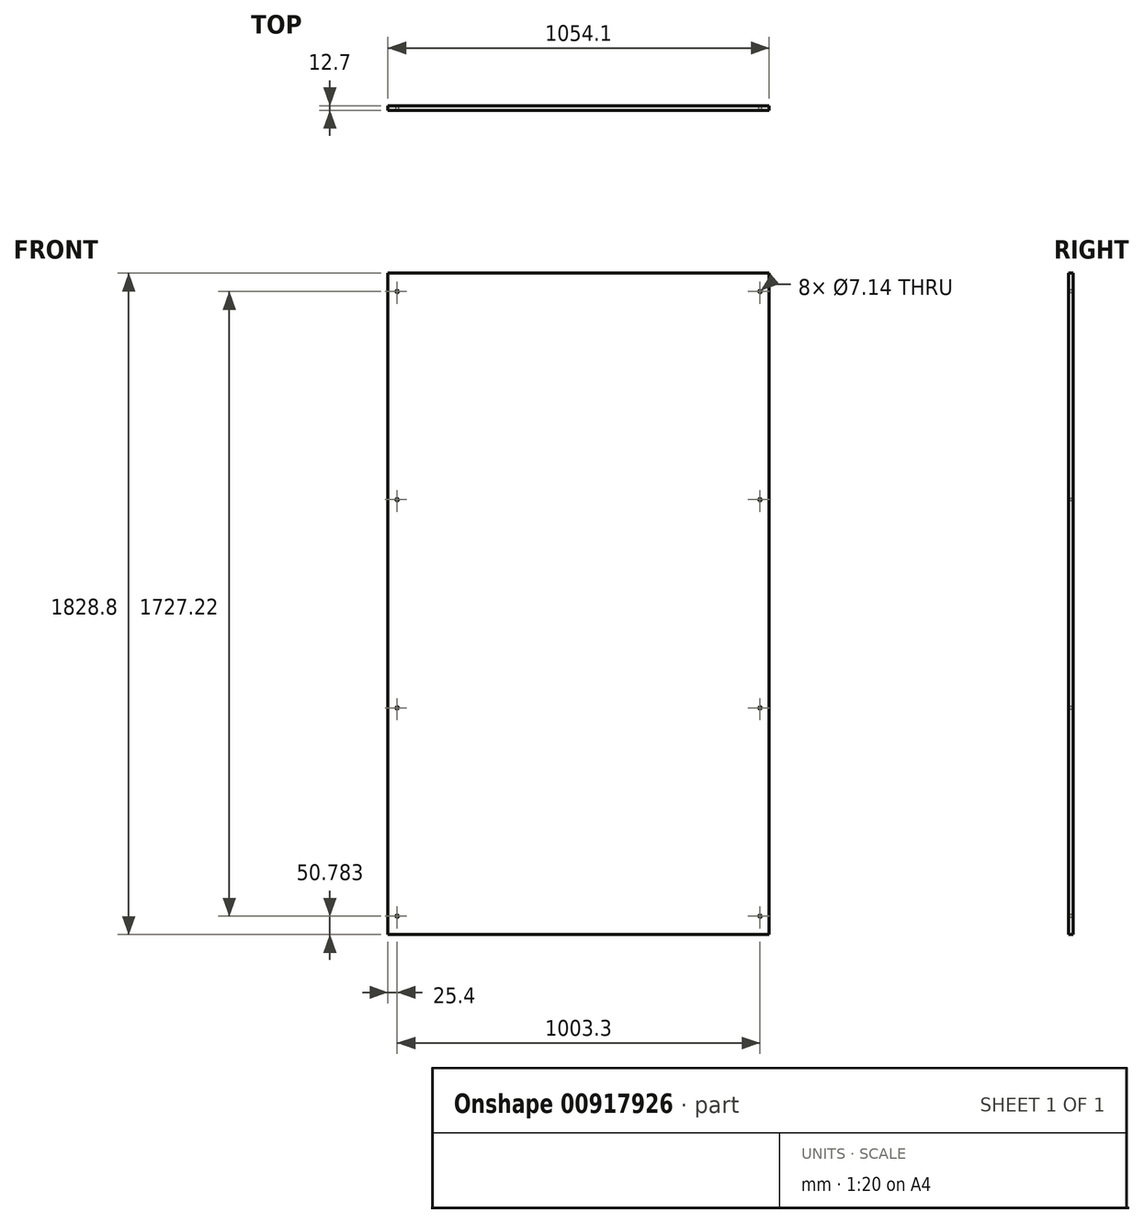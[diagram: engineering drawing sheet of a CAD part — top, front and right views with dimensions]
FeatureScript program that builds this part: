
annotation { "Feature Type Name" : "Feature", "Feature Type Description" : "" }
export const myFeature = defineFeature(function(context is Context, id is Id, definition is map)
    precondition{}
    {
        {
            var Q0;
            Q0=qCreatedBy(makeId("Front.planeOp"),FACE);
            var sketch = newSketch(context, id + "F0", { "sketchPlane" : qUnion([Q0])});
            skLineSegment(sketch, "E0.bottom", {"start": v(0, 1828.8) * mm, "end": v(1054.1, 1828.8) * mm});
            skLineSegment(sketch, "E0.top", {"start": v(0, 0) * mm, "end": v(1054.1, 0) * mm});
            skLineSegment(sketch, "E0.left", {"start": v(0, 1828.8) * mm, "end": v(0, 0) * mm});
            skLineSegment(sketch, "E0.right", {"start": v(1054.1, 1828.8) * mm, "end": v(1054.1, 0) * mm});
            skSolve(sketch);
        }
        {
            var Q0;
            Q0=makeQuery(id+"F0.imprint","IMPRINT",FACE,{"disambiguationData":[TD([[makeQuery(id+"F0.imprint","IMPRINT",EDGE,{"derivedFrom":sQuery(id+"F0.wireOp",EDGE,"E0.bottom")}),-1.0]])]});
            extrude(context, id + "F1", {"entities" : qUnion([Q0]), "depth" : 12.7 * mm, "offsetDistance" : 25.4 * mm});
        }
        {
            var Q0;
            Q0=makeQuery(id+"F1.opExtrude","CAP_FACE",FACE,{"disambiguationData":[OSD([sQuery(id+"F0.wireOp",EDGE,"E0.bottom"),sQuery(id+"F0.wireOp",EDGE,"E0.top"),sQuery(id+"F0.wireOp",EDGE,"E0.left"),sQuery(id+"F0.wireOp",EDGE,"E0.right")])],"isStart":false});
            var sketch = newSketch(context, id + "F2", { "sketchPlane" : qUnion([Q0])});
            skPoint(sketch, "E1", {"position": v(25.4, 1778) * mm});
            skPoint(sketch, "E2", {"position": v(25.4, 1202.27) * mm});
            skPoint(sketch, "E3", {"position": v(25.4, 626.52) * mm});
            skPoint(sketch, "E4", {"position": v(25.4, 50.78) * mm});
            skPoint(sketch, "E5.MirrorP", {"position": v(1028.7, 1778) * mm});
            skPoint(sketch, "E6.MirrorP", {"position": v(1028.7, 626.52) * mm});
            skPoint(sketch, "E7.MirrorP", {"position": v(1028.7, 1202.27) * mm});
            skPoint(sketch, "E8.MirrorP", {"position": v(1028.7, 50.78) * mm});
            skSolve(sketch);
        }
        {
            var Q0;
            Q0=sQuery(id+"F2.wireOp",VERTEX,"E1");
            var Q1;
            Q1=sQuery(id+"F2.wireOp",VERTEX,"E2");
            var Q2;
            Q2=sQuery(id+"F2.wireOp",VERTEX,"E3");
            var Q3;
            Q3=sQuery(id+"F2.wireOp",VERTEX,"E4");
            var Q4;
            Q4=sQuery(id+"F2.wireOp",VERTEX,"E8.MirrorP");
            var Q5;
            Q5=sQuery(id+"F2.wireOp",VERTEX,"E6.MirrorP");
            var Q6;
            Q6=sQuery(id+"F2.wireOp",VERTEX,"E7.MirrorP");
            var Q7;
            Q7=sQuery(id+"F2.wireOp",VERTEX,"E5.MirrorP");
            var Q8;
            Q8=makeQuery(id+"F1.opExtrude","SWEPT_BODY",BODY,{"disambiguationData":[OSD([sQuery(id+"F0.wireOp",EDGE,"E0.bottom"),sQuery(id+"F0.wireOp",EDGE,"E0.top"),sQuery(id+"F0.wireOp",EDGE,"E0.left"),sQuery(id+"F0.wireOp",EDGE,"E0.right")])]});
            hole(context, id + "F3", {"style" : HoleStyle.SIMPLE, "endStyle" : HoleEndStyle.THROUGH, "standardTappedOrClearance" : lookupTablePath({ "fit" : "Normal (ASME)", "standard" : "ANSI", "size" : "1/4", "type" : "Clearance" }), "standardBlindInLast" : lookupTablePath({ "fit" : "Normal", "standard" : "ANSI", "size" : "1/4", "type" : "Clearance" }), "holeDiameter" : 7.14 * mm, "majorDiameter" : 6.35 * mm, "isTappedThrough" : true, "tappedDepth" : 12.7 * mm, "tapClearance" : 3, "startFromSketch" : true, "locations" : qUnion([Q0, Q1, Q2, Q3, Q4, Q5, Q6, Q7]), "scope" : qUnion([Q8])});
        }
    });
